# Revit family: Bi34
name_source: partatom
category: Equipement spécialisé
units: mm (PartAtom-declared; Revit-internal decimal feet)

## family parameters
Autoriser la découpe dans les vues = Non
Basée sur le plan de construction = Non
Conserver l'orientation des annotations = Non
Cote de connecteur circulaire = Utiliser le diamètre
Couper avec des vides une fois chargée = Non
Numéro OmniClass = 23.40.40.14
Partagée = Non
Repère de localisation dans la pièce = Non
Titre OmniClass = Food Service Equipment
Toujours verticalement = Oui
Type d'élément = Normal

## types (1)
- 6F0282
    Altezza = 720 mm  [stored 2.3622 ft]
    Altezza allacciamento elettrico da pavimento finito = 38 mm  [stored 0.124672 ft]
    Altezza da terra raccordo acqua calda = 51 mm
    Altezza dello scarico diretto acqua da pavimento finito = 51 mm
    Base stand with door = Non
    Corrente di funzionamento normale = 10 A
    Description = MULTIPOWER DOUBLE WALL GLASS WASHER
    Diametro dello scarico diretto di acqua = 1 1/2"
    Diametro raccordo acqua calda = 1"
    Elévation par défaut = 0 mm  [stored 0 ft]
    Fabricant = COMENDA
    Fase = 3
    Frequenza = 50 Hz
    HEIGHT FROM THE FLOOR = 5 mm  [stored 0.0164042 ft]
    Lunghezza = 480 mm  [stored 1.5748 ft]
    Modèle = Bi35 R
    Numero dei poli = 3
    Peso netto = 59.00 kg
    Potenza elettrica = 6850 W
    Pressione minima acqua calda = 2000.0 Pa
    Profondità = 530 mm  [stored 1.73885 ft]
    Protezione contro le sovracorrenti = 16 A
    Stand feet kit = Non
    Temperatura raccomandata per acqua calda = 50 °C
    Tensione = 400 V
    URL = www.comenda.fr
    URL catalogo = https://comenda.fr

note: [stored X ft] marks values corroborated as IEEE doubles in the binary element streams (Revit-internal decimal feet)

## geometry (parser evidence)
native form markers: Sweep x3
no freeform markers — native parametric forms only
